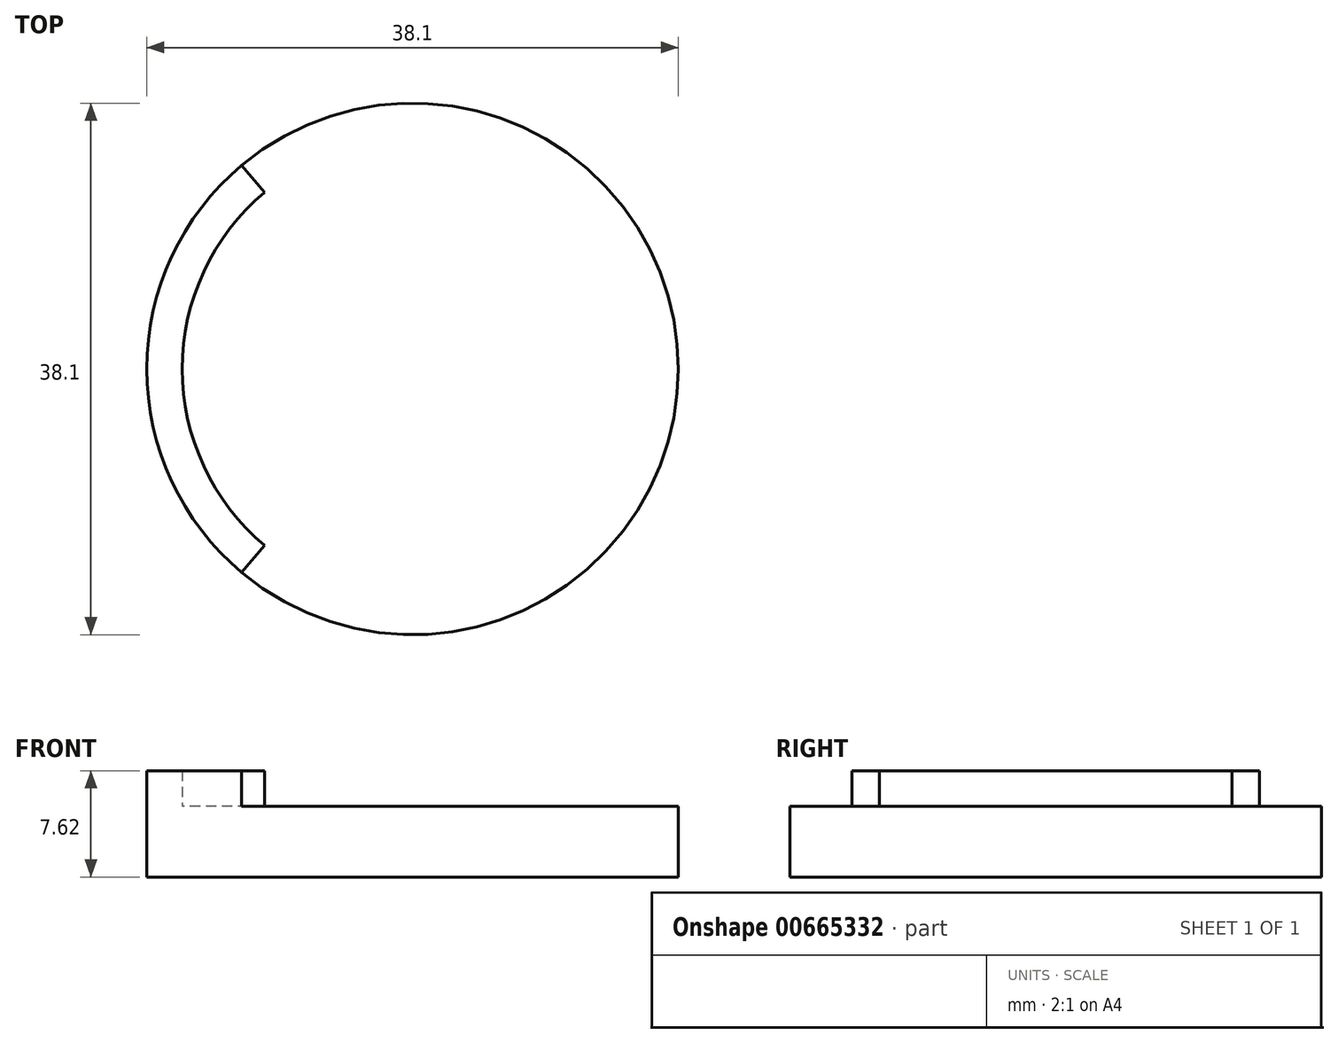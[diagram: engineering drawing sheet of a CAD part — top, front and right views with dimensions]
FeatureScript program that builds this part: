
annotation { "Feature Type Name" : "Feature", "Feature Type Description" : "" }
export const myFeature = defineFeature(function(context is Context, id is Id, definition is map)
    precondition{}
    {
        {
            var Q0;
            Q0=qCreatedBy(makeId("Top.planeOp"),FACE);
            var sketch = newSketch(context, id + "F0", { "sketchPlane" : qUnion([Q0])});
            skCircle(sketch, "E0", {"center": v(0, 0) * mm, "radius": 19.05 * mm});
            skSolve(sketch);
        }
        {
            var Q0;
            Q0=makeQuery(id+"F0.imprint","IMPRINT",FACE,{"disambiguationData":[TD([[makeQuery(id+"F0.imprint","IMPRINT",EDGE,{"derivedFrom":sQuery(id+"F0.wireOp",EDGE,"E0")}),1.0]])]});
            extrude(context, id + "F1", {"entities" : qUnion([Q0]), "depth" : 5.08 * mm, "offsetDistance" : 25.4 * mm});
        }
        {
            var Q0;
            Q0=makeQuery(id+"F1.opExtrude","CAP_FACE",FACE,{"disambiguationData":[OSD([sQuery(id+"F0.wireOp",EDGE,"E0")])],"isStart":false});
            var sketch = newSketch(context, id + "F2", { "sketchPlane" : qUnion([Q0])});
            skCircle(sketch, "E1.0", {"center": v(0, 0) * mm, "radius": 16.51 * mm});
            skLineSegment(sketch, "E2", {"start": v(0, 0) * mm, "end": v(0, 19.05) * mm, "construction": true});
            skLineSegment(sketch, "E3", {"start": v(0, 0) * mm, "end": v(-12.25, 14.6) * mm});
            skLineSegment(sketch, "E4.MirrorCS", {"start": v(0, 0) * mm, "end": v(-12.25, -14.6) * mm});
            skSolve(sketch);
        }
        {
            var Q0;
            {var subQ0=sQuery(id+"F2.wireOp",EDGE,"E3");var subQ1=sQuery(id+"F2.wireOp",EDGE,"E1.0");var subQ2=makeQuery(id+"F2.imprint","INTERSECT",VERTEX,{"derivedFrom":[subQ1,subQ0]});Q0=makeQuery(id+"F2.imprint","IMPRINT",FACE,{"disambiguationData":[TD([[makeQuery(id+"F2.imprint","IMPRINT",EDGE,{"disambiguationData":[TD([[subQ2,-1.0]])],"derivedFrom":subQ1}),-1.0]])]});}
            extrude(context, id + "F3", {"entities" : qUnion([Q0]), "operationType" : NewBodyOperationType.ADD, "depth" : 2.54 * mm, "offsetDistance" : 25.4 * mm});
        }
    });
